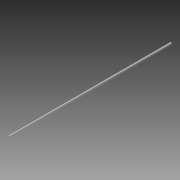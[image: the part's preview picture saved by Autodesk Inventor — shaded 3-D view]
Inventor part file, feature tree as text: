
AUTODESK INVENTOR PART (.ipt)
format: ipt  version: 2014 (Build 180170000, 170)  size: 148,480 bytes
history: native  units: in
note: dims shown in document units (in); Inventor stores cm internally (conversion verified against a paired STEP export)
features: sketch x7, hole x4, extrude x3, pattern_linear x1
ambient origin geometry x8: Origin, YZ Plane, XZ Plane, XY Plane, X Axis, Y Axis, Z Axis, Center Point
bodies: Solid1 (feature_tree)
feature tree (15):
  extrude  "Extrusion1"  Depth=0.1181in
  extrude  "Extrusion2"  Depth=19.685in TaperAngle=0.0deg
  hole  "overlap2"  [1 undecoded]
  hole  "overlap3"  [1 undecoded]
  hole  "overlap4"  [1 undecoded]
  extrude  "endHole"  Depth=0.0394in
  hole  "Hole4"  [1 undecoded]
  pattern_linear  "Rectangular Pattern1"  [2 undecoded]
  sketch  "Sketch1"  dims[d0=2.4803in d1=0.1181in]
  sketch  "Sketch2"  dims[d2=236.2205in d3=0.0in d4=19.685in d5=0.0in]
  sketch  "Sketch3"  dims[d6=0.0394in]
  sketch  "Sketch4"  dims[d7=0.0394in d8=0.2362in d9=0.1575in d10=0.0787in d11=90.0deg d12=0.315in d13=0.8108in d14=0.0394in]
  sketch  "Sketch5"  dims[d15=0.0394in d16=0.2362in d17=0.1575in d18=0.0787in d19=90.0deg d20=0.315in d21=0.8108in d22=0.0394in]
  sketch  "Sketch6"  dims[d23=0.0394in d24=0.2362in d25=0.1575in d26=0.0787in d27=90.0deg d28=0.315in d29=0.8108in d30=0.2756in]
  sketch  "Sketch7"  dims[d31=3.937in d32=0.0in d33=0.0394in d34=0.0394in d35=0.2362in d36=0.1575in d37=0.0787in d38=90.0deg d39=0.315in d40=0.8108in d41=7.0866in d43=11.811in]
note: 6 required parameter values undecoded (feature->parameter linkage not recoverable at this tier; creation-order binding heuristic only, values carry confidence <= 0.55)
